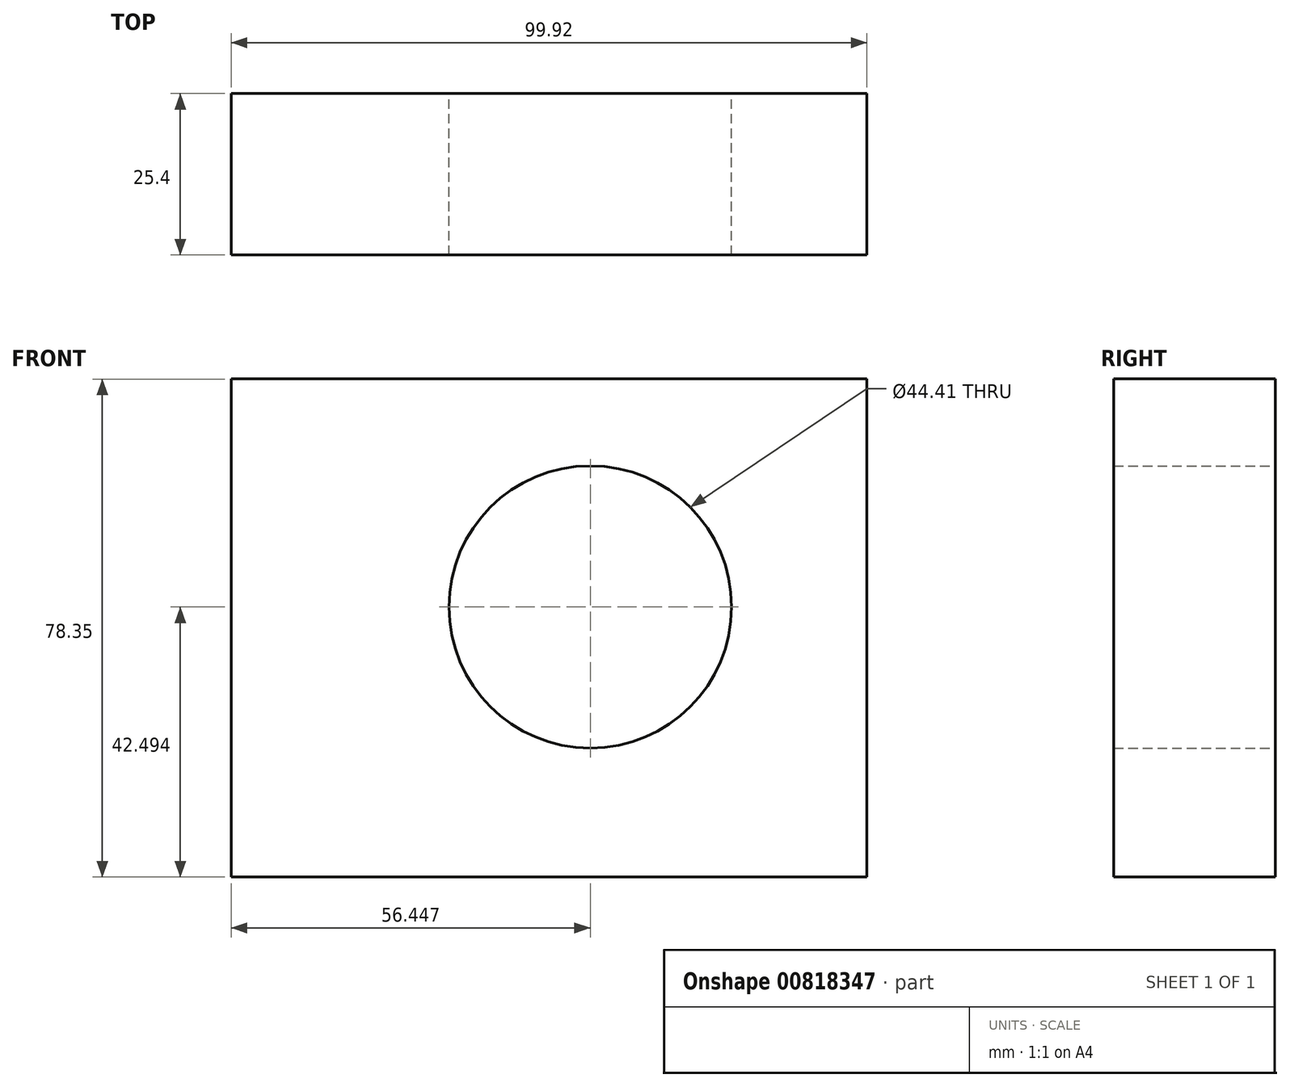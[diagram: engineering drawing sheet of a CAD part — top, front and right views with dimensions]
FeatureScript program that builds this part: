
annotation { "Feature Type Name" : "Feature", "Feature Type Description" : "" }
export const myFeature = defineFeature(function(context is Context, id is Id, definition is map)
    precondition{}
    {
        {
            var Q0;
            Q0=qCreatedBy(makeId("Front.planeOp"),FACE);
            var sketch = newSketch(context, id + "F0", { "sketchPlane" : qUnion([Q0])});
            skLineSegment(sketch, "E0.bottom", {"start": v(-46.29, 40.22) * mm, "end": v(53.63, 40.22) * mm});
            skLineSegment(sketch, "E0.top", {"start": v(-46.29, -38.13) * mm, "end": v(53.63, -38.13) * mm});
            skLineSegment(sketch, "E0.left", {"start": v(-46.29, 40.22) * mm, "end": v(-46.29, -38.13) * mm});
            skLineSegment(sketch, "E0.right", {"start": v(53.63, 40.22) * mm, "end": v(53.63, -38.13) * mm});
            skCircle(sketch, "E1", {"center": v(10.16, 4.36) * mm, "radius": 22.2 * mm});
            skPoint(sketch, "E1.first.point", {"position": v(-8.29, 16.73) * mm});
            skPoint(sketch, "E1.second.point", {"position": v(26.9, 18.95) * mm});
            skPoint(sketch, "E1.third.point", {"position": v(-6.37, -10.46) * mm});
            skSolve(sketch);
        }
        {
            var Q0;
            Q0 = qSketchRegion(id + "F0", true);
            extrude(context, id + "F1", {"entities" : qUnion([Q0]), "depth" : 25.4 * mm, "offsetDistance" : 25.4 * mm});
        }
    });
